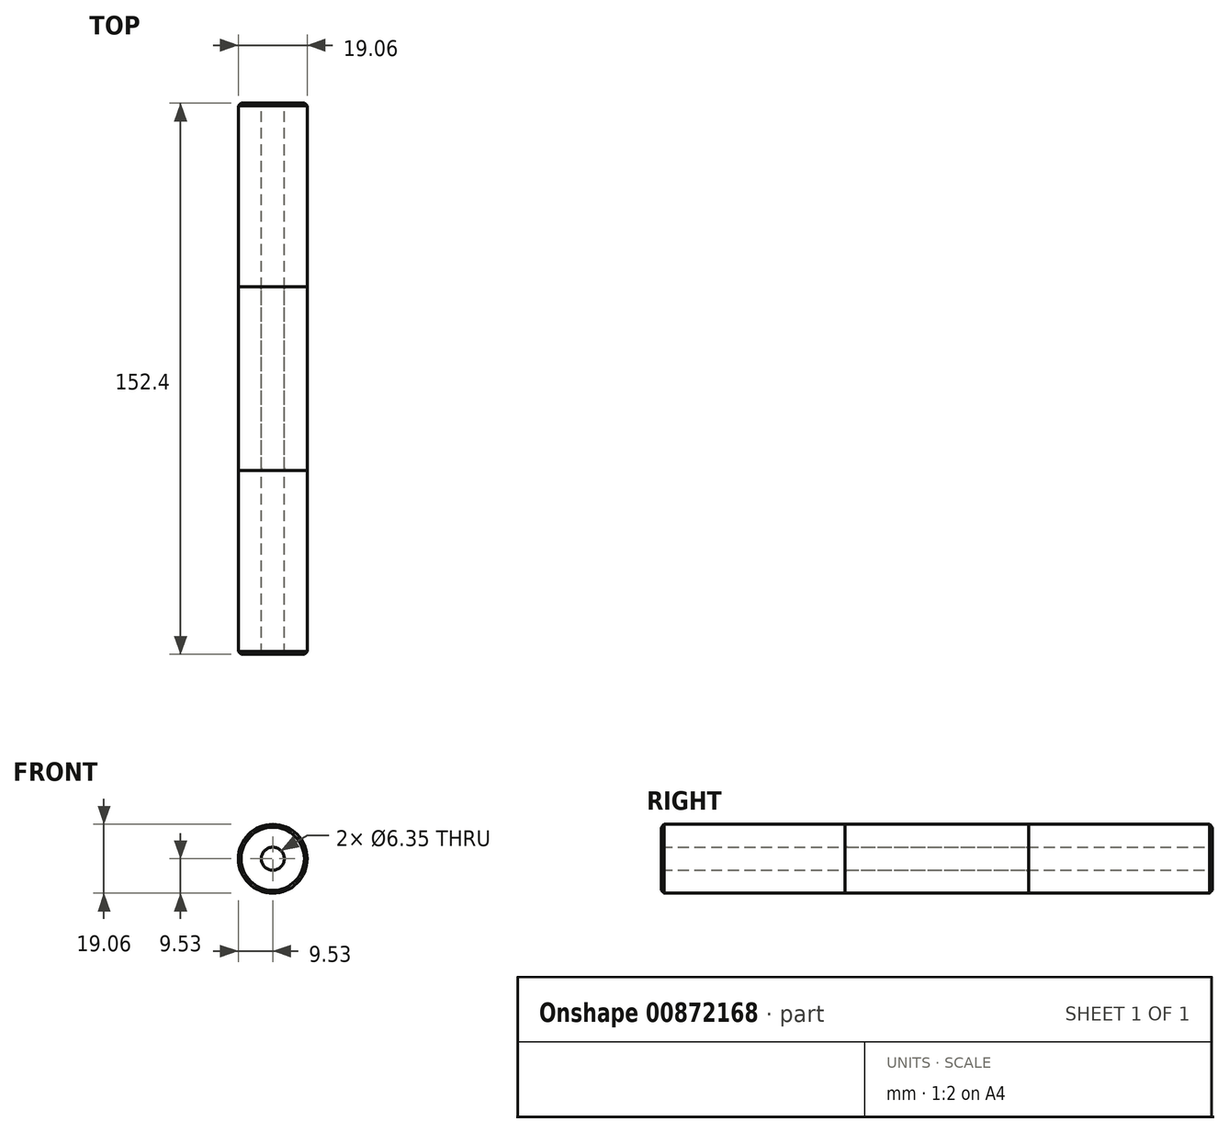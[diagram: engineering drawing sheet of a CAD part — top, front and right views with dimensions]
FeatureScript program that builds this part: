
annotation { "Feature Type Name" : "Feature", "Feature Type Description" : "" }
export const myFeature = defineFeature(function(context is Context, id is Id, definition is map)
    precondition{}
    {
        {
            var Q0;
            Q0=qCreatedBy(makeId("Front.planeOp"),FACE);
            var sketch = newSketch(context, id + "F0", { "sketchPlane" : qUnion([Q0])});
            skLineSegment(sketch, "E0", {"start": v(-25.4, 0) * mm, "end": v(25.4, 0) * mm});
            skLineSegment(sketch, "E1", {"start": v(25.4, 0) * mm, "end": v(25.4, 22.21) * mm});
            skLineSegment(sketch, "E2", {"start": v(-25.4, 0) * mm, "end": v(-25.4, 22.21) * mm});
            skCircle(sketch, "E3", {"center": v(0, 0) * mm, "radius": 9.53 * mm});
            skCircle(sketch, "E4", {"center": v(0, 0) * mm, "radius": 3.18 * mm});
            skSolve(sketch);
        }
        {
            var Q0;
            Q0=qSketchRegion(id+"F0",true);
            var Q1;
            Q1=sQuery(id+"F0.wireOp",EDGE,"E3");
            extrude(context, id + "F1", {"entities" : qUnion([Q0]), "surfaceEntities" : qUnion([Q1]), "endBound" : BoundingType.SYMMETRIC, "depth" : 152.4 * mm, "offsetDistance" : 25.4 * mm});
        }
        {
            var Q0;
            Q0=makeQuery(id+"F1.opExtrude","CAP_EDGE",EDGE,{"disambiguationData":[OSD([sQuery(id+"F0.wireOp",EDGE,"E3")])],"isStart":true});
            var Q1;
            Q1=makeQuery(id+"F1.opExtrude","CAP_EDGE",EDGE,{"disambiguationData":[OSD([sQuery(id+"F0.wireOp",EDGE,"E3")])],"isStart":false});
            chamfer(context, id + "F2", {"entities" : qUnion([Q0, Q1]), "width" : 0.8 * mm, "tangentPropagation" : true});
        }
        {
            var Q0;
            {var subQ0=sQuery(id+"F0.wireOp",EDGE,"E4");var subQ1=sQuery(id+"F0.wireOp",EDGE,"E0");var subQ2=makeQuery(id+"F0.imprint","INTERSECT",VERTEX,{"disambiguationData":[OD(0.0)],"derivedFrom":[subQ1,subQ0]});Q0=makeQuery(id+"F0.imprint","IMPRINT",FACE,{"disambiguationData":[TD([[makeQuery(id+"F0.imprint","IMPRINT",EDGE,{"disambiguationData":[TD([[subQ2,-1.0]])],"derivedFrom":subQ1}),1.0]])]});}
            var Q1;
            {var subQ0=sQuery(id+"F0.wireOp",EDGE,"E4");var subQ1=sQuery(id+"F0.wireOp",EDGE,"E0");var subQ2=makeQuery(id+"F0.imprint","INTERSECT",VERTEX,{"disambiguationData":[OD(0.0)],"derivedFrom":[subQ1,subQ0]});Q1=makeQuery(id+"F0.imprint","IMPRINT",FACE,{"disambiguationData":[TD([[makeQuery(id+"F0.imprint","IMPRINT",EDGE,{"disambiguationData":[TD([[subQ2,-1.0]])],"derivedFrom":subQ1}),-1.0]])]});}
            var Q2;
            Q2=sQuery(id+"F0.wireOp",EDGE,"E4");
            extrude(context, id + "F3", {"entities" : qUnion([Q0, Q1]), "surfaceEntities" : qUnion([Q2]), "endBound" : BoundingType.SYMMETRIC, "depth" : 50.8 * mm, "offsetDistance" : 25.4 * mm});
        }
        {
            var Q0;
            Q0=makeQuery(id+"F3.opExtrude","CAP_EDGE",EDGE,{"disambiguationData":[OSD([sQuery(id+"F0.wireOp",EDGE,"E4")])],"isStart":false});
            var Q1;
            Q1=makeQuery(id+"F3.opExtrude","CAP_EDGE",EDGE,{"disambiguationData":[OSD([sQuery(id+"F0.wireOp",EDGE,"E4")])],"isStart":true});
            fillet(context, id + "F4", {"entities" : qUnion([Q0, Q1]), "radius" : 0.76 * mm, "tangentPropagation" : true, "allowEdgeOverflow" : false});
        }
    });
